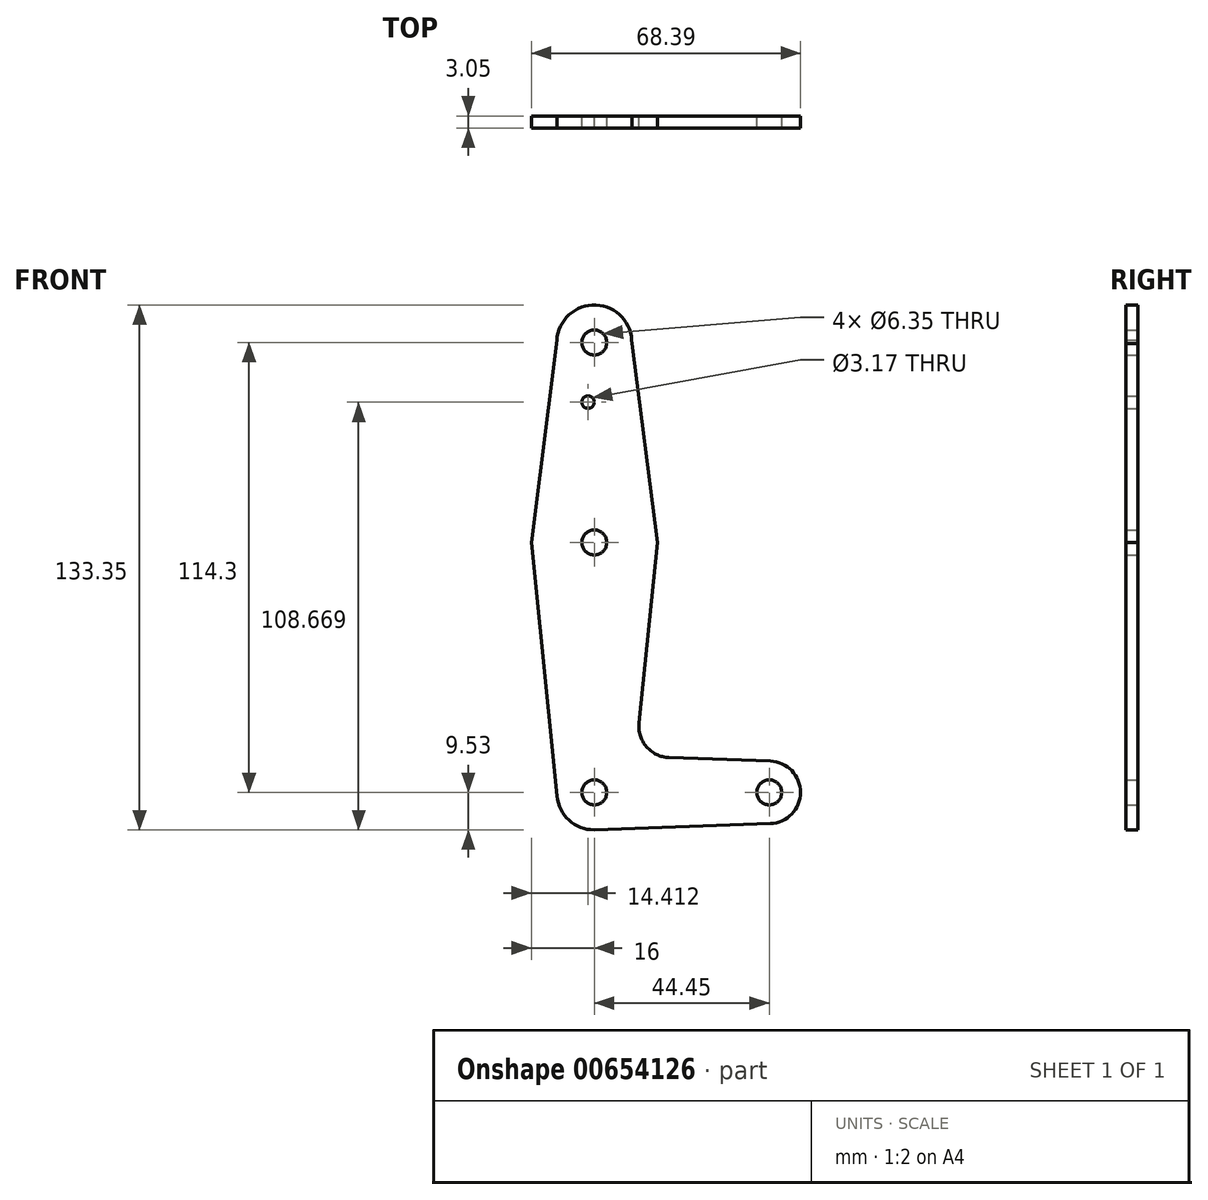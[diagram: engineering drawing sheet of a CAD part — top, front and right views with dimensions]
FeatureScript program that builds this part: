
annotation { "Feature Type Name" : "Feature", "Feature Type Description" : "" }
export const myFeature = defineFeature(function(context is Context, id is Id, definition is map)
    precondition{}
    {
        {
            var Q0;
            Q0=qCreatedBy(makeId("Front.planeOp"),FACE);
            var sketch = newSketch(context, id + "F0", { "sketchPlane" : qUnion([Q0])});
            skLineSegment(sketch, "E0", {"start": v(0, 50.8) * mm, "end": v(0, -63.5) * mm});
            skLineSegment(sketch, "E1", {"start": v(0, -63.5) * mm, "end": v(44.45, -63.5) * mm});
            skCircle(sketch, "E2", {"center": v(0, 50.8) * mm, "radius": 9.53 * mm});
            skCircle(sketch, "E3", {"center": v(0, 0) * mm, "radius": 15.88 * mm});
            skCircle(sketch, "E4", {"center": v(44.45, -63.5) * mm, "radius": 7.94 * mm});
            skCircle(sketch, "E5", {"center": v(0, -63.5) * mm, "radius": 9.53 * mm});
            skLineSegment(sketch, "E6", {"start": v(0, 50.8) * mm, "end": v(0, 0) * mm});
            skLineSegment(sketch, "E7", {"start": v(0, 0) * mm, "end": v(0, -63.5) * mm});
            skLineSegment(sketch, "E8", {"start": v(-9.5, 51.36) * mm, "end": v(-16, 0) * mm});
            skLineSegment(sketch, "E9", {"start": v(9.52, 50.48) * mm, "end": v(16, 0) * mm});
            skLineSegment(sketch, "E10", {"start": v(16, 0) * mm, "end": v(11.36, -45.9) * mm});
            skLineSegment(sketch, "E11", {"start": v(-16, 0) * mm, "end": v(-9.48, -64.46) * mm});
            skLineSegment(sketch, "E12", {"start": v(0, -73.03) * mm, "end": v(44.73, -71.43) * mm});
            skLineSegment(sketch, "E13", {"start": v(18.98, -54.65) * mm, "end": v(44.73, -55.57) * mm});
            skCircle(sketch, "E14", {"center": v(-1.59, 35.64) * mm, "radius": 1.59 * mm});
            skCircle(sketch, "E15", {"center": v(0, 50.8) * mm, "radius": 3.18 * mm});
            skCircle(sketch, "E16", {"center": v(0, 0) * mm, "radius": 3.18 * mm});
            skCircle(sketch, "E17", {"center": v(0, -63.5) * mm, "radius": 3.18 * mm});
            skCircle(sketch, "E18", {"center": v(44.45, -63.5) * mm, "radius": 3.18 * mm});
            skPoint(sketch, "E19.newPointA", {"position": v(0, -53.97) * mm});
            skArc(sketch, "E19.filletArc", {"start": v(11.36, -45.9) * mm, "mid": v(13.27, -51.93) * mm, "end": v(18.98, -54.65) * mm});
            skSolve(sketch);
        }
        {
            var Q0;
            {var subQ0=sQuery(id+"F0.wireOp",EDGE,"E12");var subQ1=sQuery(id+"F0.wireOp",EDGE,"E5");var subQ2=makeQuery(id+"F0.imprint","INTERSECT",VERTEX,{"disambiguationData":[OD(0.0)],"derivedFrom":[subQ1,subQ0]});Q0=makeQuery(id+"F0.imprint","IMPRINT",FACE,{"disambiguationData":[TD([[makeQuery(id+"F0.imprint","IMPRINT",EDGE,{"disambiguationData":[TD([[subQ2,-1.0]])],"derivedFrom":subQ1}),1.0]])]});}
            var Q1;
            {var subQ0=sQuery(id+"F0.wireOp",EDGE,"E4");var subQ1=sQuery(id+"F0.wireOp",EDGE,"E1");var subQ2=makeQuery(id+"F0.imprint","INTERSECT",VERTEX,{"derivedFrom":[subQ1,subQ0]});Q1=makeQuery(id+"F0.imprint","IMPRINT",FACE,{"disambiguationData":[TD([[makeQuery(id+"F0.imprint","IMPRINT",EDGE,{"disambiguationData":[TD([[subQ2,1.0]])],"derivedFrom":subQ1}),-1.0]])]});}
            var Q2;
            Q2=makeQuery(id+"F0.imprint","IMPRINT",FACE,{"disambiguationData":[TD([[makeQuery(id+"F0.imprint","IMPRINT",EDGE,{"derivedFrom":sQuery(id+"F0.wireOp",EDGE,"E15")}),-1.0]])]});
            var Q3;
            {var subQ5=sQuery(id+"F0.wireOp",EDGE,"E11");Q3=makeQuery(id+"F0.imprint","IMPRINT",FACE,{"disambiguationData":[TD([[makeQuery(id+"F0.imprint","IMPRINT",EDGE,{"derivedFrom":subQ5}),1.0]])]});}
            var Q4;
            Q4=makeQuery(id+"F0.imprint","IMPRINT",FACE,{"disambiguationData":[TD([[makeQuery(id+"F0.imprint","IMPRINT",EDGE,{"derivedFrom":sQuery(id+"F0.wireOp",EDGE,"E18")}),-1.0]])]});
            var Q5;
            {var subQ0=sQuery(id+"F0.wireOp",EDGE,"E14");Q5=makeQuery(id+"F0.imprint","IMPRINT",FACE,{"disambiguationData":[TD([[makeQuery(id+"F0.imprint","IMPRINT",EDGE,{"derivedFrom":subQ0}),-1.0]])]});}
            var Q6;
            {var subQ1=sQuery(id+"F0.wireOp",EDGE,"E3");var subQ8=makeQuery(id+"F0.imprint","INTERSECT",VERTEX,{"derivedFrom":[subQ1,sQuery(id+"F0.wireOp",EDGE,"E8")]});Q6=makeQuery(id+"F0.imprint","IMPRINT",FACE,{"disambiguationData":[TD([[makeQuery(id+"F0.imprint","IMPRINT",EDGE,{"disambiguationData":[TD([[subQ8,1.0]])],"derivedFrom":subQ1}),1.0]])]});}
            var Q7;
            {var subQ3=sQuery(id+"F0.wireOp",EDGE,"E1");var subQ9=sQuery(id+"F0.wireOp",EDGE,"E17");var subQ11=makeQuery(id+"F0.imprint","INTERSECT",VERTEX,{"derivedFrom":[subQ3,subQ9]});Q7=makeQuery(id+"F0.imprint","IMPRINT",FACE,{"disambiguationData":[TD([[makeQuery(id+"F0.imprint","IMPRINT",EDGE,{"disambiguationData":[TD([[subQ11,-1.0]])],"derivedFrom":subQ3}),-1.0]])]});}
            var Q8;
            {var subQ12=sQuery(id+"F0.wireOp",EDGE,"E10");Q8=makeQuery(id+"F0.imprint","IMPRINT",FACE,{"disambiguationData":[TD([[makeQuery(id+"F0.imprint","IMPRINT",EDGE,{"derivedFrom":subQ12}),-1.0]])]});}
            var Q9;
            {var subQ1=sQuery(id+"F0.wireOp",EDGE,"E3");var subQ8=makeQuery(id+"F0.imprint","INTERSECT",VERTEX,{"derivedFrom":[subQ1,sQuery(id+"F0.wireOp",EDGE,"E9")]});Q9=makeQuery(id+"F0.imprint","IMPRINT",FACE,{"disambiguationData":[TD([[makeQuery(id+"F0.imprint","IMPRINT",EDGE,{"disambiguationData":[TD([[subQ8,-1.0]])],"derivedFrom":subQ1}),1.0]])]});}
            var Q10;
            {var subQ1=sQuery(id+"F0.wireOp",EDGE,"E2");var subQ4=sQuery(id+"F0.wireOp",EDGE,"E9");var subQ5=makeQuery(id+"F0.imprint","INTERSECT",VERTEX,{"derivedFrom":[subQ1,subQ4]});Q10=makeQuery(id+"F0.imprint","IMPRINT",FACE,{"disambiguationData":[TD([[makeQuery(id+"F0.imprint","IMPRINT",EDGE,{"disambiguationData":[TD([[subQ5,1.0]])],"derivedFrom":subQ1}),-1.0]])]});}
            var Q11;
            {var subQ0=sQuery(id+"F0.wireOp",EDGE,"E17");var subQ1=sQuery(id+"F0.wireOp",EDGE,"E1");var subQ2=makeQuery(id+"F0.imprint","INTERSECT",VERTEX,{"derivedFrom":[subQ1,subQ0]});Q11=makeQuery(id+"F0.imprint","IMPRINT",FACE,{"disambiguationData":[TD([[makeQuery(id+"F0.imprint","IMPRINT",EDGE,{"disambiguationData":[TD([[subQ2,-1.0]])],"derivedFrom":subQ1}),1.0]])]});}
            extrude(context, id + "F1", {"entities" : qUnion([Q0, Q1, Q2, Q3, Q4, Q5, Q6, Q7, Q8, Q9, Q10, Q11]), "depth" : 3.05 * mm, "offsetDistance" : 25.4 * mm});
        }
    });
